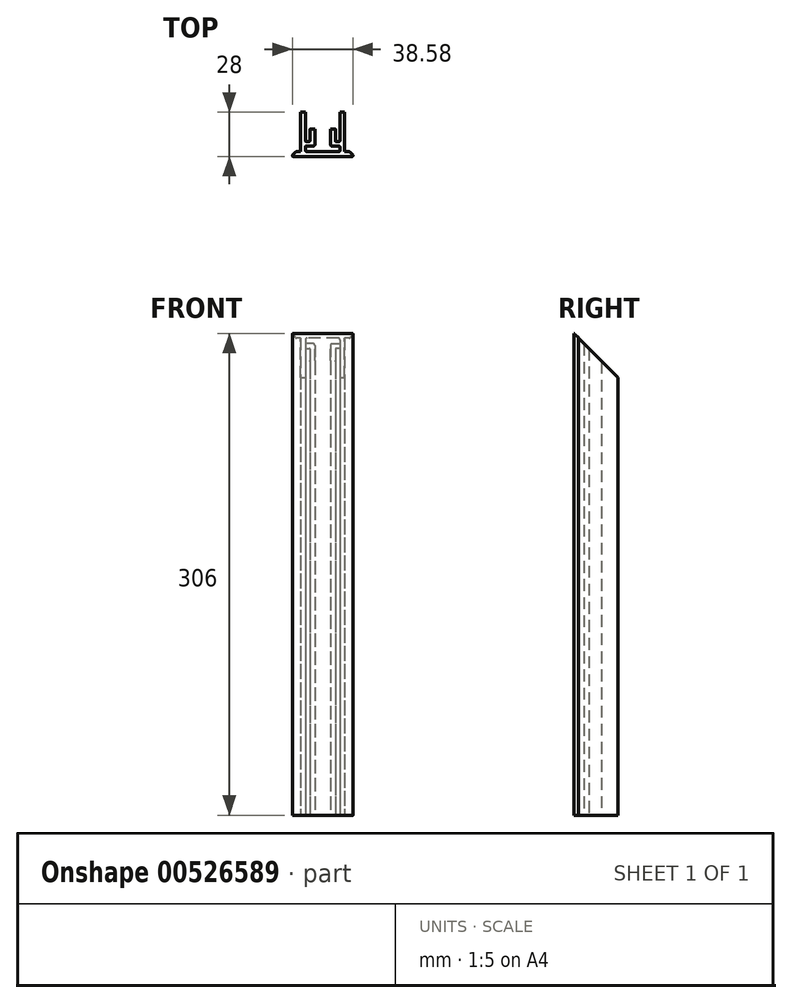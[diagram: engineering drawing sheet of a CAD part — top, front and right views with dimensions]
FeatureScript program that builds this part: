
annotation { "Feature Type Name" : "Feature", "Feature Type Description" : "" }
export const myFeature = defineFeature(function(context is Context, id is Id, definition is map)
    precondition{}
    {
        {
            var Q0;
            Q0=qCreatedBy(makeId("Top.planeOp"),FACE);
            var sketch = newSketch(context, id + "F0", { "sketchPlane" : qUnion([Q0])});
            skLineSegment(sketch, "E0", {"start": v(0, 37.2) * mm, "end": v(0, -38.8) * mm, "construction": true});
            skLineSegment(sketch, "E1", {"start": v(-30.9, 0) * mm, "end": v(40.1, 0) * mm, "construction": true});
            skLineSegment(sketch, "E2.bottom", {"start": v(-17, 0.5) * mm, "end": v(17, 0.5) * mm});
            skLineSegment(sketch, "E2.top", {"start": v(-20, -2.5) * mm, "end": v(20, -2.5) * mm});
            skLineSegment(sketch, "E3", {"start": v(-20, -2.5) * mm, "end": v(-17, 0.5) * mm});
            skLineSegment(sketch, "E4.MirrorCS", {"start": v(20, -2.5) * mm, "end": v(17, 0.5) * mm});
            skLineSegment(sketch, "E5", {"start": v(14, 0.5) * mm, "end": v(14, 25.5) * mm});
            skLineSegment(sketch, "E6", {"start": v(14, 25.5) * mm, "end": v(11, 25.5) * mm});
            skLineSegment(sketch, "E7", {"start": v(11, 25.5) * mm, "end": v(11, 0.5) * mm});
            skLineSegment(sketch, "E8.MirrorCS", {"start": v(-14, 25.5) * mm, "end": v(-11, 25.5) * mm});
            skLineSegment(sketch, "E9.MirrorCS", {"start": v(-14, 0.5) * mm, "end": v(-14, 25.5) * mm});
            skLineSegment(sketch, "E10.MirrorCS", {"start": v(-11, 25.5) * mm, "end": v(-11, 0.5) * mm});
            skLineSegment(sketch, "E11", {"start": v(11, 4) * mm, "end": v(5, 4) * mm});
            skLineSegment(sketch, "E12", {"start": v(5, 4) * mm, "end": v(5, 7) * mm});
            skLineSegment(sketch, "E13", {"start": v(5, 7) * mm, "end": v(5, 15) * mm});
            skLineSegment(sketch, "E14", {"start": v(5, 15) * mm, "end": v(8, 15) * mm});
            skLineSegment(sketch, "E15", {"start": v(8, 15) * mm, "end": v(8, 7) * mm});
            skLineSegment(sketch, "E16", {"start": v(8, 7) * mm, "end": v(11, 7) * mm});
            skLineSegment(sketch, "E17.MirrorCS", {"start": v(-5, 15) * mm, "end": v(-8, 15) * mm});
            skLineSegment(sketch, "E18.MirrorCS", {"start": v(-8, 7) * mm, "end": v(-11, 7) * mm});
            skLineSegment(sketch, "E19.MirrorCS", {"start": v(-5, 7) * mm, "end": v(-5, 15) * mm});
            skLineSegment(sketch, "E20.MirrorCS", {"start": v(-11, 4) * mm, "end": v(-5, 4) * mm});
            skLineSegment(sketch, "E21.MirrorCS", {"start": v(-8, 15) * mm, "end": v(-8, 7) * mm});
            skLineSegment(sketch, "E22.MirrorCS", {"start": v(-5, 4) * mm, "end": v(-5, 7) * mm});
            skSolve(sketch);
        }
        {
            var Q0;
            Q0=qSketchRegion(id+"F0",true);
            extrude(context, id + "F1", {"entities" : qUnion([Q0]), "depth" : 306 * mm, "offsetDistance" : 25 * mm, "symmetric" : true});
        }
        {
            var Q0;
            Q0=qCreatedBy(makeId("Right.planeOp"),FACE);
            var sketch = newSketch(context, id + "F2", { "sketchPlane" : qUnion([Q0])});
            skLineSegment(sketch, "E23.0", {"start": v(0.5, 153) * mm, "end": v(25.5, 153) * mm});
            skLineSegment(sketch, "E23.1", {"start": v(-2.5, 153) * mm, "end": v(0.5, 153) * mm});
            skLineSegment(sketch, "E24", {"start": v(-2.5, 153) * mm, "end": v(25.5, 125) * mm});
            skLineSegment(sketch, "E25", {"start": v(25.5, 125) * mm, "end": v(25.5, 153) * mm});
            skSolve(sketch);
        }
        {
            var Q0;
            Q0=qSketchRegion(id+"F2",true);
            extrude(context, id + "F3", {"entities" : qUnion([Q0]), "operationType" : NewBodyOperationType.REMOVE, "oppositeDirection" : true, "depth" : 60 * mm, "symmetric" : true});
        }
        {
            var Q0;
            Q0=makeQuery(id+"F1.opExtrude","SWEPT_EDGE",EDGE,{"disambiguationData":[OSD([sQuery(id+"F0.wireOp",EDGE,"E2.bottom"),sQuery(id+"F0.wireOp",EDGE,"E4.MirrorCS")])]});
            var Q1;
            {var subQ0=sQuery(id+"F2.wireOp",EDGE,"E24");Q1=makeQuery(id+"F3.boolean.opBoolean","COPY",EDGE,{"disambiguationData":[topologyDisambiguationEdgeConnected([makeQuery(id+"F1.opExtrude","SWEPT_FACE",FACE,{"disambiguationData":[OSD([sQuery(id+"F0.wireOp",EDGE,"E6")])]})])],"derivedFrom":makeQuery(id+"F3.opExtrude","SWEPT_EDGE",EDGE,{"disambiguationData":[OSD([subQ0,sQuery(id+"F2.wireOp",EDGE,"E25")])]})});}
            var Q2;
            Q2=makeQuery(id+"F1.opExtrude","SWEPT_EDGE",EDGE,{"disambiguationData":[OSD([sQuery(id+"F0.wireOp",EDGE,"E2.bottom"),sQuery(id+"F0.wireOp",EDGE,"E10.MirrorCS")])]});
            var Q3;
            {var subQ0=sQuery(id+"F2.wireOp",EDGE,"E24");Q3=makeQuery(id+"F3.boolean.opBoolean","COPY",EDGE,{"disambiguationData":[topologyDisambiguationEdgeConnected([makeQuery(id+"F1.opExtrude","SWEPT_FACE",FACE,{"disambiguationData":[OSD([sQuery(id+"F0.wireOp",EDGE,"E8.MirrorCS")])]})])],"derivedFrom":makeQuery(id+"F3.opExtrude","SWEPT_EDGE",EDGE,{"disambiguationData":[OSD([subQ0,sQuery(id+"F2.wireOp",EDGE,"E25")])]})});}
            var Q4;
            Q4=makeQuery(id+"F1.opExtrude","SWEPT_EDGE",EDGE,{"disambiguationData":[OSD([sQuery(id+"F0.wireOp",EDGE,"E2.bottom"),sQuery(id+"F0.wireOp",EDGE,"E3")])]});
            var Q5;
            Q5=makeQuery(id+"F1.opExtrude","SWEPT_EDGE",EDGE,{"disambiguationData":[OSD([sQuery(id+"F0.wireOp",EDGE,"E2.bottom"),sQuery(id+"F0.wireOp",EDGE,"E7")])]});
            var Q6;
            {var subQ0=sQuery(id+"F2.wireOp",EDGE,"E24");Q6=makeQuery(id+"FuO8uSxEj4nSnSF_1.1.F3.boolean.opBoolean","COPY",EDGE,{"disambiguationData":[topologyDisambiguationEdgeConnected([makeQuery(id+"F1.opExtrude","SWEPT_FACE",FACE,{"disambiguationData":[OSD([sQuery(id+"F0.wireOp",EDGE,"E8.MirrorCS")])]})])],"derivedFrom":makeQuery(id+"FuO8uSxEj4nSnSF_1.1.F3.opExtrude","SWEPT_EDGE",EDGE,{"disambiguationData":[OSD([subQ0,sQuery(id+"F2.wireOp",EDGE,"E25")])]})});}
            var Q7;
            {var subQ0=sQuery(id+"F2.wireOp",EDGE,"E24");Q7=makeQuery(id+"FuO8uSxEj4nSnSF_1.1.F3.boolean.opBoolean","COPY",EDGE,{"disambiguationData":[topologyDisambiguationEdgeConnected([makeQuery(id+"F1.opExtrude","SWEPT_FACE",FACE,{"disambiguationData":[OSD([sQuery(id+"F0.wireOp",EDGE,"E6")])]})])],"derivedFrom":makeQuery(id+"FuO8uSxEj4nSnSF_1.1.F3.opExtrude","SWEPT_EDGE",EDGE,{"disambiguationData":[OSD([subQ0,sQuery(id+"F2.wireOp",EDGE,"E25")])]})});}
            fillet(context, id + "F4", {"entities" : qUnion([Q0, Q1, Q2, Q3, Q4, Q5, Q6, Q7]), "radius" : 1 * mm, "tangentPropagation" : true, "allowEdgeOverflow" : false});
        }
        {
            var Q0;
            Q0=makeQuery(id+"FuO8uSxEj4nSnSF_1.1.F3.boolean.opBoolean","INTERSECT",EDGE,{"derivedFrom":[makeQuery(id+"F1.opExtrude","SWEPT_FACE",FACE,{"disambiguationData":[OSD([sQuery(id+"F0.wireOp",EDGE,"E14")])]}),makeQuery(id+"FuO8uSxEj4nSnSF_1.1.F3.opExtrude","SWEPT_FACE",FACE,{"disambiguationData":[OSD([sQuery(id+"F2.wireOp",EDGE,"E24")])]})]});
            var Q1;
            Q1=makeQuery(id+"FuO8uSxEj4nSnSF_1.1.F3.boolean.opBoolean","INTERSECT",EDGE,{"derivedFrom":[makeQuery(id+"F1.opExtrude","SWEPT_FACE",FACE,{"disambiguationData":[OSD([sQuery(id+"F0.wireOp",EDGE,"E17.MirrorCS")])]}),makeQuery(id+"FuO8uSxEj4nSnSF_1.1.F3.opExtrude","SWEPT_FACE",FACE,{"disambiguationData":[OSD([sQuery(id+"F2.wireOp",EDGE,"E24")])]})]});
            var Q2;
            Q2=makeQuery(id+"F3.boolean.opBoolean","INTERSECT",EDGE,{"derivedFrom":[makeQuery(id+"F1.opExtrude","SWEPT_FACE",FACE,{"disambiguationData":[OSD([sQuery(id+"F0.wireOp",EDGE,"E17.MirrorCS")])]}),makeQuery(id+"F3.opExtrude","SWEPT_FACE",FACE,{"disambiguationData":[OSD([sQuery(id+"F2.wireOp",EDGE,"E24")])]})]});
            var Q3;
            Q3=makeQuery(id+"F3.boolean.opBoolean","INTERSECT",EDGE,{"derivedFrom":[makeQuery(id+"F1.opExtrude","SWEPT_FACE",FACE,{"disambiguationData":[OSD([sQuery(id+"F0.wireOp",EDGE,"E14")])]}),makeQuery(id+"F3.opExtrude","SWEPT_FACE",FACE,{"disambiguationData":[OSD([sQuery(id+"F2.wireOp",EDGE,"E24")])]})]});
            var Q4;
            Q4=makeQuery(id+"F1.opExtrude","SWEPT_EDGE",EDGE,{"disambiguationData":[OSD([sQuery(id+"F0.wireOp",EDGE,"E11"),sQuery(id+"F0.wireOp",EDGE,"E12")])]});
            var Q5;
            Q5=makeQuery(id+"F1.opExtrude","SWEPT_EDGE",EDGE,{"disambiguationData":[OSD([sQuery(id+"F0.wireOp",EDGE,"E22.MirrorCS"),sQuery(id+"F0.wireOp",EDGE,"E20.MirrorCS")])]});
            fillet(context, id + "F5", {"entities" : qUnion([Q0, Q1, Q2, Q3, Q4, Q5]), "radius" : 1 * mm, "tangentPropagation" : true, "allowEdgeOverflow" : false});
        }
        {
            var Q0;
            Q0=makeQuery(id+"F1.opExtrude","SWEPT_EDGE",EDGE,{"disambiguationData":[OSD([sQuery(id+"F0.wireOp",EDGE,"E18.MirrorCS"),sQuery(id+"F0.wireOp",EDGE,"E21.MirrorCS")])]});
            var Q1;
            Q1=makeQuery(id+"F1.opExtrude","SWEPT_EDGE",EDGE,{"disambiguationData":[OSD([sQuery(id+"F0.wireOp",EDGE,"E10.MirrorCS"),sQuery(id+"F0.wireOp",EDGE,"E18.MirrorCS")])]});
            var Q2;
            Q2=makeQuery(id+"F1.opExtrude","SWEPT_EDGE",EDGE,{"disambiguationData":[OSD([sQuery(id+"F0.wireOp",EDGE,"E10.MirrorCS"),sQuery(id+"F0.wireOp",EDGE,"E20.MirrorCS")])]});
            var Q3;
            Q3=makeQuery(id+"F1.opExtrude","SWEPT_EDGE",EDGE,{"disambiguationData":[OSD([sQuery(id+"F0.wireOp",EDGE,"E7"),sQuery(id+"F0.wireOp",EDGE,"E11")])]});
            var Q4;
            Q4=makeQuery(id+"F1.opExtrude","SWEPT_EDGE",EDGE,{"disambiguationData":[OSD([sQuery(id+"F0.wireOp",EDGE,"E7"),sQuery(id+"F0.wireOp",EDGE,"E16")])]});
            var Q5;
            Q5=makeQuery(id+"F1.opExtrude","SWEPT_EDGE",EDGE,{"disambiguationData":[OSD([sQuery(id+"F0.wireOp",EDGE,"E15"),sQuery(id+"F0.wireOp",EDGE,"E16")])]});
            fillet(context, id + "F6", {"entities" : qUnion([Q0, Q1, Q2, Q3, Q4, Q5]), "radius" : 0.5 * mm, "tangentPropagation" : true, "allowEdgeOverflow" : false});
        }
        {
            var Q0;
            Q0=makeQuery(id+"F1.opExtrude","SWEPT_EDGE",EDGE,{"disambiguationData":[OSD([sQuery(id+"F0.wireOp",EDGE,"E2.top"),sQuery(id+"F0.wireOp",EDGE,"E4.MirrorCS")])]});
            var Q1;
            Q1=makeQuery(id+"F1.opExtrude","SWEPT_EDGE",EDGE,{"disambiguationData":[OSD([sQuery(id+"F0.wireOp",EDGE,"E2.top"),sQuery(id+"F0.wireOp",EDGE,"E3")])]});
            fillet(context, id + "F7", {"entities" : qUnion([Q0, Q1]), "radius" : 0.5 * mm, "tangentPropagation" : true, "allowEdgeOverflow" : false});
        }
    });
